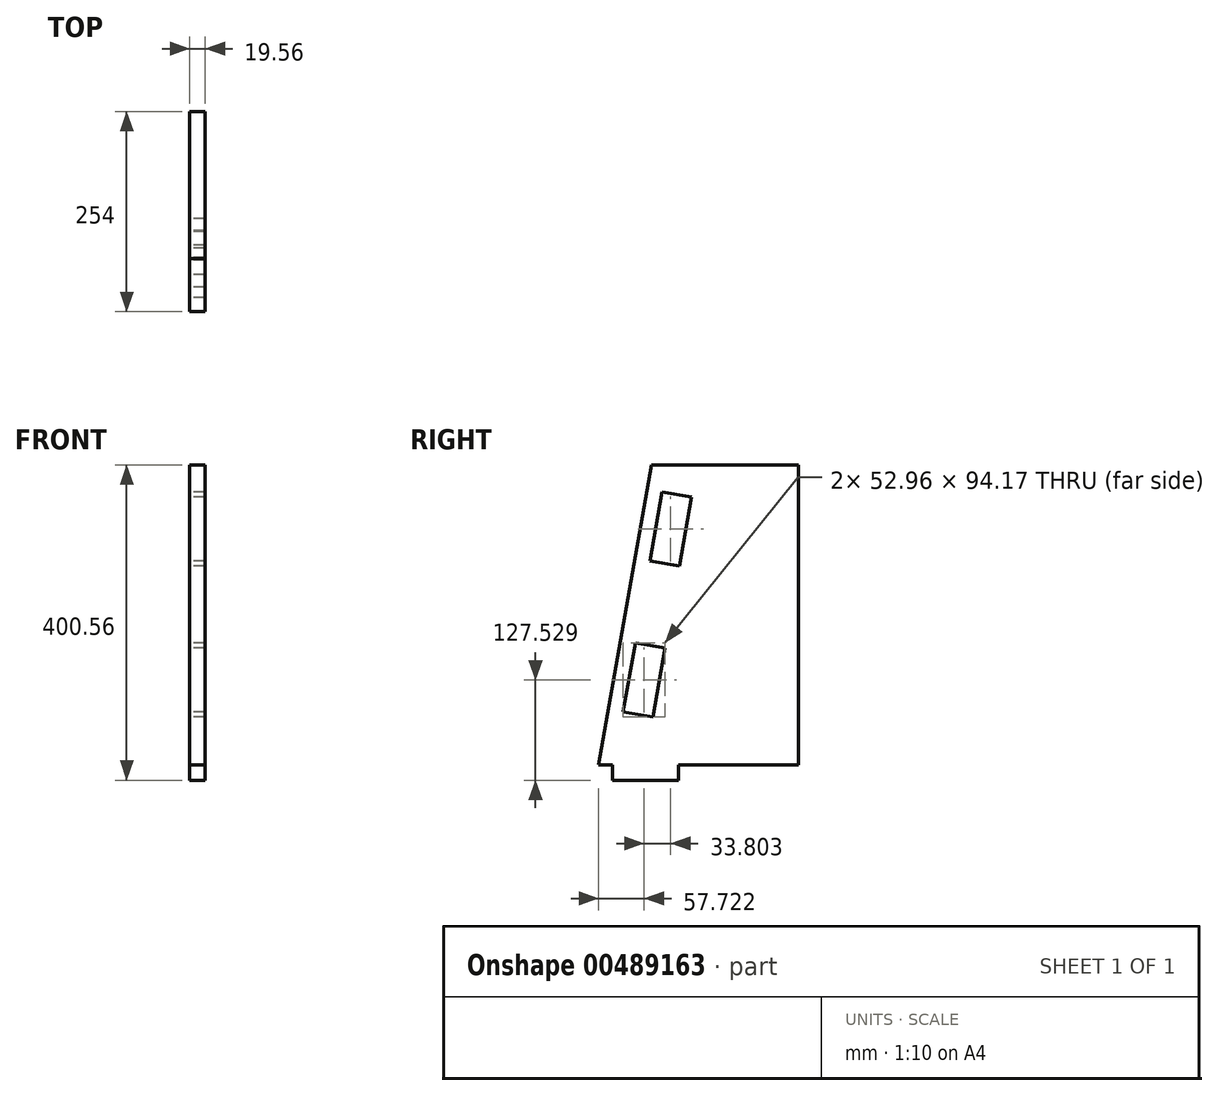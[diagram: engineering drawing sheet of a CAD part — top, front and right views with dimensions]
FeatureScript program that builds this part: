
annotation { "Feature Type Name" : "Feature", "Feature Type Description" : "" }
export const myFeature = defineFeature(function(context is Context, id is Id, definition is map)
    precondition{}
    {
        {
            var Q0;
            Q0=qCreatedBy(makeId("Right.planeOp"),FACE);
            var sketch = newSketch(context, id + "F0", { "sketchPlane" : qUnion([Q0])});
            skLineSegment(sketch, "E0", {"start": v(-85.13, -212.4) * mm, "end": v(-17.95, -212.4) * mm});
            skLineSegment(sketch, "E1", {"start": v(-17.95, 168.6) * mm, "end": v(-85.13, -212.4) * mm});
            skLineSegment(sketch, "E2.bottom", {"start": v(-17.95, 168.6) * mm, "end": v(168.87, 168.6) * mm});
            skLineSegment(sketch, "E2.top", {"start": v(-17.95, -212.4) * mm, "end": v(168.87, -212.4) * mm});
            skLineSegment(sketch, "E2.right", {"start": v(168.87, 168.6) * mm, "end": v(168.87, -212.4) * mm});
            skLineSegment(sketch, "E3.bottom", {"start": v(-67.35, -212.4) * mm, "end": v(16.47, -212.4) * mm});
            skLineSegment(sketch, "E3.top", {"start": v(-67.35, -231.95) * mm, "end": v(16.47, -231.95) * mm});
            skLineSegment(sketch, "E3.left", {"start": v(-67.35, -212.4) * mm, "end": v(-67.35, -231.95) * mm});
            skLineSegment(sketch, "E3.right", {"start": v(16.47, -212.4) * mm, "end": v(16.47, -231.95) * mm});
            skLineSegment(sketch, "E4.bottom", {"start": v(67.27, -212.4) * mm, "end": v(151.09, -212.4) * mm});
            skLineSegment(sketch, "E4.top", {"start": v(67.27, -231.95) * mm, "end": v(151.09, -231.95) * mm});
            skLineSegment(sketch, "E4.left", {"start": v(67.27, -212.4) * mm, "end": v(67.27, -231.95) * mm});
            skLineSegment(sketch, "E4.right", {"start": v(151.09, -212.4) * mm, "end": v(151.09, -231.95) * mm});
            skLineSegment(sketch, "E5", {"start": v(17.44, 40.2) * mm, "end": v(32.87, 127.75) * mm});
            skLineSegment(sketch, "E6", {"start": v(-4.65, 134.37) * mm, "end": v(-20.08, 46.82) * mm});
            skLineSegment(sketch, "E7", {"start": v(-4.65, 134.37) * mm, "end": v(32.87, 127.75) * mm});
            skLineSegment(sketch, "E8", {"start": v(-20.08, 46.82) * mm, "end": v(17.44, 40.2) * mm});
            skLineSegment(sketch, "E9", {"start": v(-16.37, -151.5) * mm, "end": v(-0.93, -63.95) * mm});
            skLineSegment(sketch, "E10", {"start": v(-53.89, -144.89) * mm, "end": v(-38.45, -57.34) * mm});
            skLineSegment(sketch, "E11", {"start": v(-38.45, -57.34) * mm, "end": v(-0.93, -63.95) * mm});
            skLineSegment(sketch, "E12", {"start": v(-53.89, -144.89) * mm, "end": v(-16.37, -151.5) * mm});
            skSolve(sketch);
        }
        {
            var Q0;
            {var subQ0=sQuery(id+"F0.wireOp",EDGE,"E0");Q0=makeQuery(id+"F0.imprint","IMPRINT",FACE,{"disambiguationData":[TD([[makeQuery(id+"F0.imprint","IMPRINT",EDGE,{"derivedFrom":subQ0}),1.0]])]});}
            var Q1;
            Q1=makeQuery(id+"F0.imprint","IMPRINT",FACE,{"disambiguationData":[TD([[makeQuery(id+"F0.imprint","IMPRINT",EDGE,{"derivedFrom":sQuery(id+"F0.wireOp",EDGE,"E2.bottom")}),-1.0]])]});
            var Q2;
            Q2=makeQuery(id+"F0.imprint","IMPRINT",FACE,{"disambiguationData":[TD([[makeQuery(id+"F0.imprint","IMPRINT",EDGE,{"derivedFrom":sQuery(id+"F0.wireOp",EDGE,"E3.top")}),1.0]])]});
            var Q3;
            Q3=makeQuery(id+"F0.imprint","IMPRINT",FACE,{"disambiguationData":[TD([[makeQuery(id+"F0.imprint","IMPRINT",EDGE,{"derivedFrom":sQuery(id+"F0.wireOp",EDGE,"E4.bottom")}),-1.0]])]});
            extrude(context, id + "F1", {"entities" : qUnion([Q0, Q1, Q2, Q3]), "depth" : 19.56 * mm, "offsetDistance" : 25.4 * mm});
        }
    });
